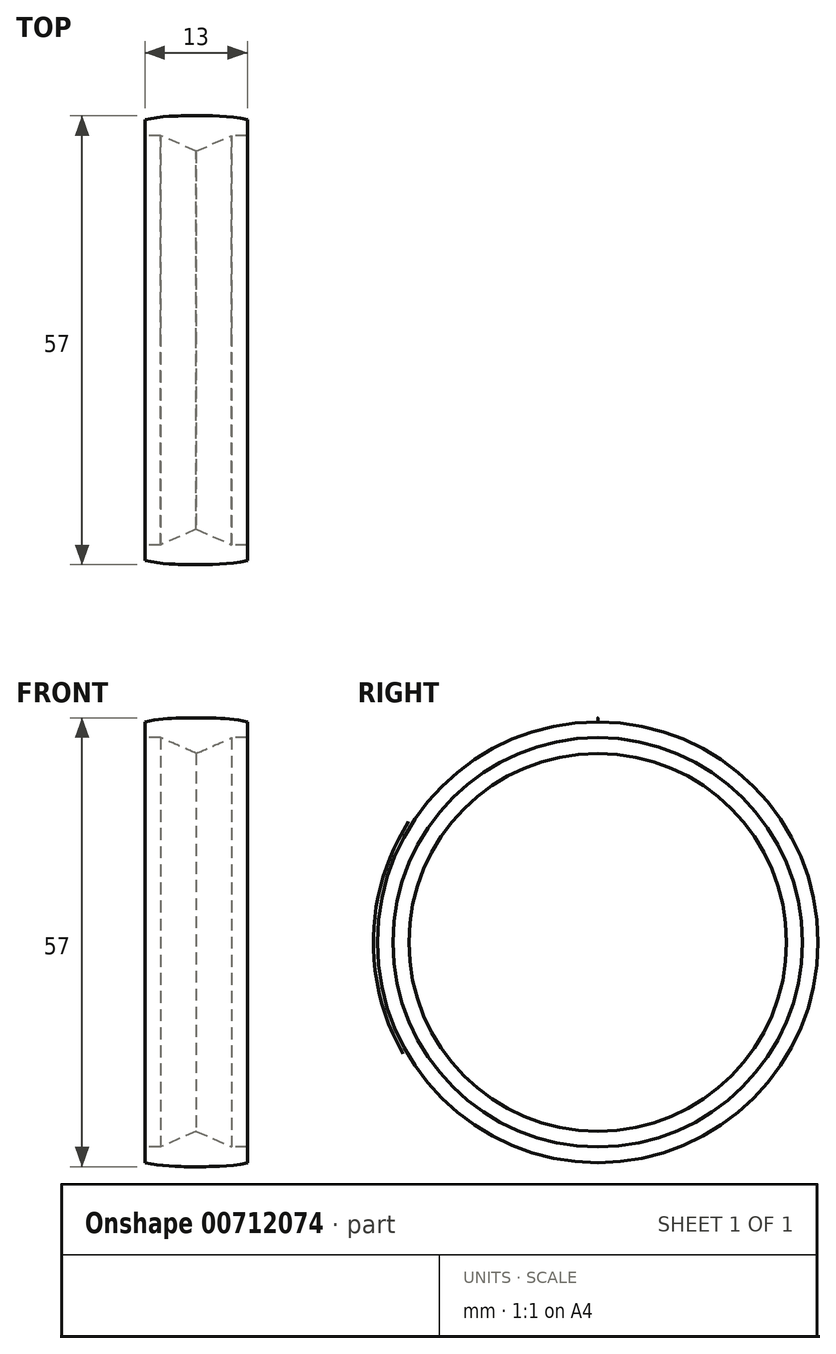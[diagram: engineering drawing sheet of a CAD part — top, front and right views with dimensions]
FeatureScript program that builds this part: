
annotation { "Feature Type Name" : "Feature", "Feature Type Description" : "" }
export const myFeature = defineFeature(function(context is Context, id is Id, definition is map)
    precondition{}
    {
        {
            var Q0;
            Q0=qCreatedBy(makeId("Right.planeOp"),FACE);
            var sketch = newSketch(context, id + "F0", { "sketchPlane" : qUnion([Q0])});
            skLineSegment(sketch, "E0", {"start": v(0, 0) * mm, "end": v(0, 26) * mm, "construction": true});
            skSolve(sketch);
        }
        {
            var Q0;
            Q0=qCreatedBy(makeId("Front.planeOp"),FACE);
            var sketch = newSketch(context, id + "F1", { "sketchPlane" : qUnion([Q0])});
            skLineSegment(sketch, "E1", {"start": v(0, 26) * mm, "end": v(2, 26) * mm});
            skLineSegment(sketch, "E2", {"start": v(2, 26) * mm, "end": v(6.5, 24) * mm});
            skLineSegment(sketch, "E3", {"start": v(6.5, 24) * mm, "end": v(11, 26) * mm});
            skLineSegment(sketch, "E4", {"start": v(11, 26) * mm, "end": v(13, 26) * mm});
            skLineSegment(sketch, "E5", {"start": v(0, 26) * mm, "end": v(0, 28) * mm});
            skLineSegment(sketch, "E6", {"start": v(13, 26) * mm, "end": v(13, 28) * mm});
            skLineSegment(sketch, "E7", {"start": v(6.5, 24) * mm, "end": v(6.5, 28.5) * mm, "construction": true});
            skFitSpline(sketch, "E8", {"points": [v(0, 28) * mm, v(6.5, 28.5) * mm, v(13, 28) * mm], "startDerivative": vector(13, 3) * mm, "endDerivative": vector(13, -3) * mm});
            skLineSegment(sketch, "E9", {"start": v(0, 0) * mm, "end": v(28, 0) * mm, "construction": true});
            skSolve(sketch);
        }
        {
            var Q0;
            Q0=makeQuery(id+"F1.imprint","IMPRINT",FACE,{"disambiguationData":[TD([[makeQuery(id+"F1.imprint","IMPRINT",EDGE,{"derivedFrom":sQuery(id+"F1.wireOp",EDGE,"E1")}),1.0]])]});
            var Q1;
            Q1=sQuery(id+"F1.wireOp",EDGE,"E9");
            revolve(context, id + "F2", {"surfaceOperationType" : NewSurfaceOperationType.NEW, "entities" : qUnion([Q0]), "axis" : qUnion([Q1]), "revolveType" : RevolveType.FULL});
        }
    });
